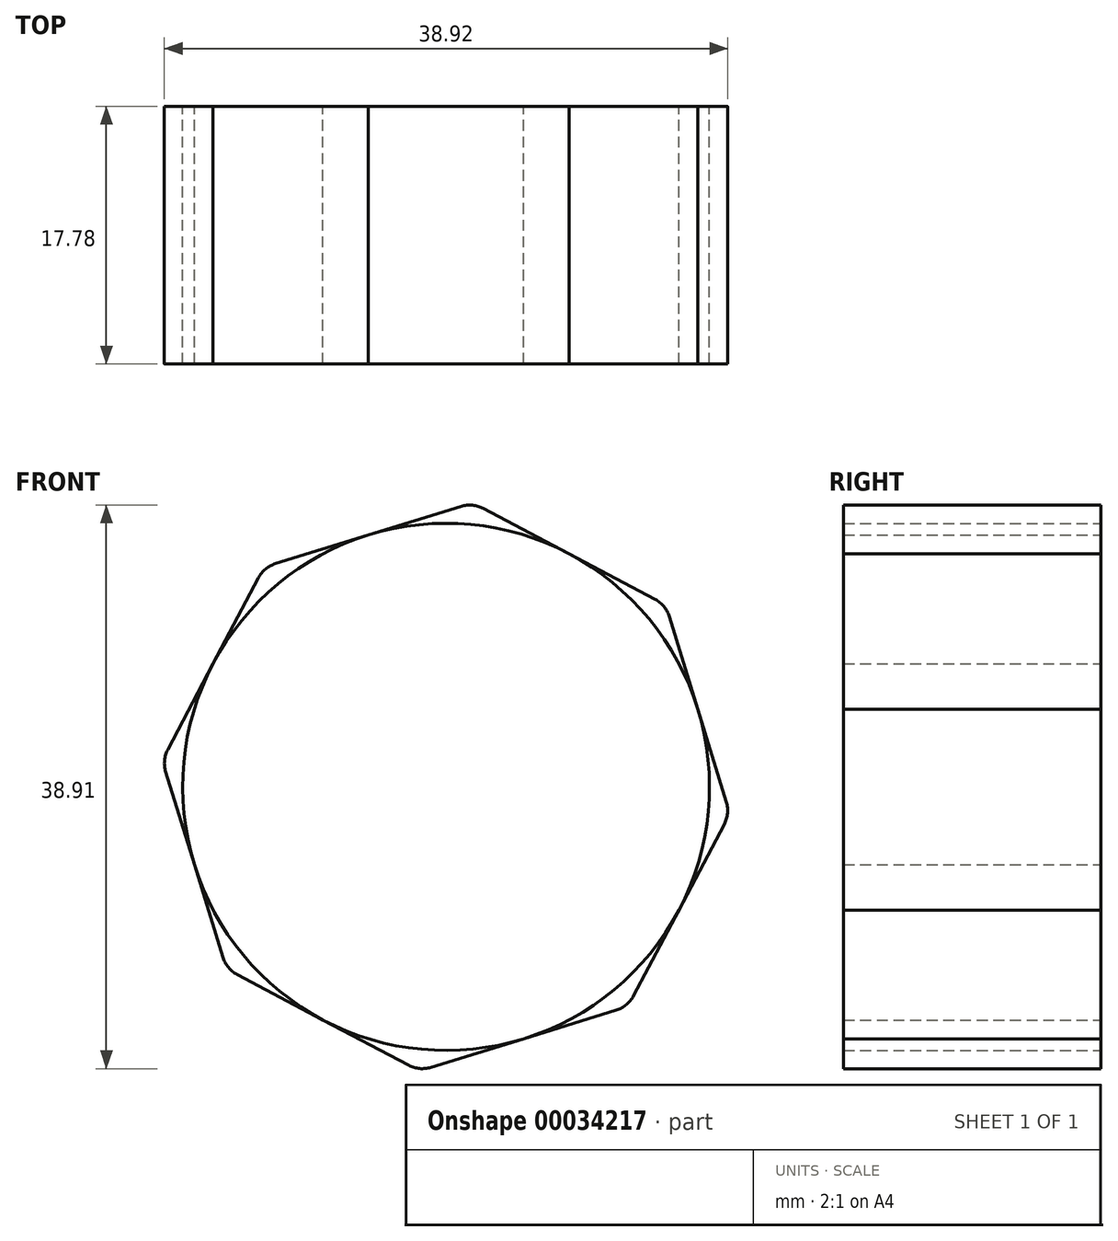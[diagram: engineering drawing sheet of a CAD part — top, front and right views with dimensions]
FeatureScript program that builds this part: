
annotation { "Feature Type Name" : "Feature", "Feature Type Description" : "" }
export const myFeature = defineFeature(function(context is Context, id is Id, definition is map)
    precondition{}
    {
        {
            var Q0;
            Q0=qCreatedBy(makeId("Front.planeOp"),FACE);
            var sketch = newSketch(context, id + "F0", { "sketchPlane" : qUnion([Q0])});
            skCircle(sketch, "E0.cCircle", {"center": v(-11.84, 26.18) * mm, "radius": 18.2 * mm, "construction": true});
            skLineSegment(sketch, "E0.0", {"start": v(3.33, 38.74) * mm, "end": v(7.77, 24.34) * mm});
            skLineSegment(sketch, "E0.1", {"start": v(7.77, 24.34) * mm, "end": v(0.73, 11) * mm});
            skLineSegment(sketch, "E0.2", {"start": v(0.73, 11) * mm, "end": v(-13.68, 6.57) * mm});
            skLineSegment(sketch, "E0.3", {"start": v(-13.68, 6.57) * mm, "end": v(-27, 13.6) * mm});
            skLineSegment(sketch, "E0.4", {"start": v(-27, 13.6) * mm, "end": v(-31.45, 28.01) * mm});
            skLineSegment(sketch, "E0.5", {"start": v(-31.45, 28.01) * mm, "end": v(-24.4, 41.34) * mm});
            skLineSegment(sketch, "E0.6", {"start": v(-24.4, 41.34) * mm, "end": v(-10, 45.79) * mm});
            skLineSegment(sketch, "E0.7", {"start": v(-10, 45.79) * mm, "end": v(3.33, 38.74) * mm});
            skPoint(sketch, "E0.0.midPoint", {"position": v(5.55, 31.54) * mm});
            skCircle(sketch, "E1", {"center": v(-11.84, 26.18) * mm, "radius": 18.2 * mm});
            skSolve(sketch);
        }
        {
            var Q0;
            {var subQ1=sQuery(id+"F0.wireOp",EDGE,"E0.5");var subQ3=sQuery(id+"F0.wireOp",EDGE,"E0.4");var subQ5=makeQuery(id+"F0.imprint","INTERSECT",VERTEX,{"derivedFrom":[subQ3,subQ1]});Q0=makeQuery(id+"F0.imprint","IMPRINT",FACE,{"disambiguationData":[TD([[makeQuery(id+"F0.imprint","IMPRINT",EDGE,{"disambiguationData":[TD([[subQ5,1.0]])],"derivedFrom":subQ3}),-1.0]])]});}
            var Q1;
            {var subQ1=sQuery(id+"F0.wireOp",EDGE,"E0.4");var subQ3=sQuery(id+"F0.wireOp",EDGE,"E0.3");var subQ5=makeQuery(id+"F0.imprint","INTERSECT",VERTEX,{"derivedFrom":[subQ3,subQ1]});Q1=makeQuery(id+"F0.imprint","IMPRINT",FACE,{"disambiguationData":[TD([[makeQuery(id+"F0.imprint","IMPRINT",EDGE,{"disambiguationData":[TD([[subQ5,1.0]])],"derivedFrom":subQ3}),-1.0]])]});}
            var Q2;
            {var subQ1=sQuery(id+"F0.wireOp",EDGE,"E0.3");var subQ3=sQuery(id+"F0.wireOp",EDGE,"E0.2");var subQ5=makeQuery(id+"F0.imprint","INTERSECT",VERTEX,{"derivedFrom":[subQ3,subQ1]});Q2=makeQuery(id+"F0.imprint","IMPRINT",FACE,{"disambiguationData":[TD([[makeQuery(id+"F0.imprint","IMPRINT",EDGE,{"disambiguationData":[TD([[subQ5,1.0]])],"derivedFrom":subQ3}),-1.0]])]});}
            var Q3;
            {var subQ1=sQuery(id+"F0.wireOp",EDGE,"E0.2");var subQ3=sQuery(id+"F0.wireOp",EDGE,"E0.1");var subQ5=makeQuery(id+"F0.imprint","INTERSECT",VERTEX,{"derivedFrom":[subQ3,subQ1]});Q3=makeQuery(id+"F0.imprint","IMPRINT",FACE,{"disambiguationData":[TD([[makeQuery(id+"F0.imprint","IMPRINT",EDGE,{"disambiguationData":[TD([[subQ5,1.0]])],"derivedFrom":subQ3}),-1.0]])]});}
            var Q4;
            {var subQ1=sQuery(id+"F0.wireOp",EDGE,"E0.1");var subQ3=sQuery(id+"F0.wireOp",EDGE,"E0.0");var subQ5=makeQuery(id+"F0.imprint","INTERSECT",VERTEX,{"derivedFrom":[subQ3,subQ1]});Q4=makeQuery(id+"F0.imprint","IMPRINT",FACE,{"disambiguationData":[TD([[makeQuery(id+"F0.imprint","IMPRINT",EDGE,{"disambiguationData":[TD([[subQ5,1.0]])],"derivedFrom":subQ3}),-1.0]])]});}
            var Q5;
            {var subQ1=sQuery(id+"F0.wireOp",EDGE,"E0.7");var subQ3=sQuery(id+"F0.wireOp",EDGE,"E0.0");var subQ5=makeQuery(id+"F0.imprint","INTERSECT",VERTEX,{"derivedFrom":[subQ3,subQ1]});Q5=makeQuery(id+"F0.imprint","IMPRINT",FACE,{"disambiguationData":[TD([[makeQuery(id+"F0.imprint","IMPRINT",EDGE,{"disambiguationData":[TD([[subQ5,-1.0]])],"derivedFrom":subQ3}),-1.0]])]});}
            var Q6;
            {var subQ1=sQuery(id+"F0.wireOp",EDGE,"E0.7");var subQ3=sQuery(id+"F0.wireOp",EDGE,"E0.6");var subQ5=makeQuery(id+"F0.imprint","INTERSECT",VERTEX,{"derivedFrom":[subQ3,subQ1]});Q6=makeQuery(id+"F0.imprint","IMPRINT",FACE,{"disambiguationData":[TD([[makeQuery(id+"F0.imprint","IMPRINT",EDGE,{"disambiguationData":[TD([[subQ5,1.0]])],"derivedFrom":subQ3}),-1.0]])]});}
            var Q7;
            {var subQ0=sQuery(id+"F0.wireOp",EDGE,"E0.6");var subQ3=sQuery(id+"F0.wireOp",EDGE,"E0.5");var subQ4=makeQuery(id+"F0.imprint","INTERSECT",VERTEX,{"derivedFrom":[subQ3,subQ0]});Q7=makeQuery(id+"F0.imprint","IMPRINT",FACE,{"disambiguationData":[TD([[makeQuery(id+"F0.imprint","IMPRINT",EDGE,{"disambiguationData":[TD([[subQ4,1.0]])],"derivedFrom":subQ3}),-1.0]])]});}
            extrude(context, id + "F1", {"entities" : qUnion([Q0, Q1, Q2, Q3, Q4, Q5, Q6, Q7]), "endBound" : BoundingType.SYMMETRIC, "depth" : 17.78 * mm});
        }
        {
            var Q0;
            Q0=makeQuery(id+"F1.opExtrude","SWEPT_EDGE",EDGE,{"disambiguationData":[OSD([sQuery(id+"F0.wireOp",EDGE,"E0.4"),sQuery(id+"F0.wireOp",EDGE,"E0.5")])]});
            var Q1;
            Q1=makeQuery(id+"F1.opExtrude","SWEPT_EDGE",EDGE,{"disambiguationData":[OSD([sQuery(id+"F0.wireOp",EDGE,"E0.5"),sQuery(id+"F0.wireOp",EDGE,"E0.6")])]});
            var Q2;
            Q2=makeQuery(id+"F1.opExtrude","SWEPT_EDGE",EDGE,{"disambiguationData":[OSD([sQuery(id+"F0.wireOp",EDGE,"E0.6"),sQuery(id+"F0.wireOp",EDGE,"E0.7")])]});
            var Q3;
            Q3=makeQuery(id+"F1.opExtrude","SWEPT_EDGE",EDGE,{"disambiguationData":[OSD([sQuery(id+"F0.wireOp",EDGE,"E0.3"),sQuery(id+"F0.wireOp",EDGE,"E0.4")])]});
            var Q4;
            Q4=makeQuery(id+"F1.opExtrude","SWEPT_EDGE",EDGE,{"disambiguationData":[OSD([sQuery(id+"F0.wireOp",EDGE,"E0.2"),sQuery(id+"F0.wireOp",EDGE,"E0.3")])]});
            var Q5;
            Q5=makeQuery(id+"F1.opExtrude","SWEPT_EDGE",EDGE,{"disambiguationData":[OSD([sQuery(id+"F0.wireOp",EDGE,"E0.1"),sQuery(id+"F0.wireOp",EDGE,"E0.2")])]});
            var Q6;
            Q6=makeQuery(id+"F1.opExtrude","SWEPT_EDGE",EDGE,{"disambiguationData":[OSD([sQuery(id+"F0.wireOp",EDGE,"E0.0"),sQuery(id+"F0.wireOp",EDGE,"E0.1")])]});
            var Q7;
            Q7=makeQuery(id+"F1.opExtrude","SWEPT_EDGE",EDGE,{"disambiguationData":[OSD([sQuery(id+"F0.wireOp",EDGE,"E0.0"),sQuery(id+"F0.wireOp",EDGE,"E0.7")])]});
            fillet(context, id + "F2", {"entities" : qUnion([Q0, Q1, Q2, Q3, Q4, Q5, Q6, Q7]), "radius" : 2 * mm, "tangentPropagation" : true, "allowEdgeOverflow" : false});
        }
    });
